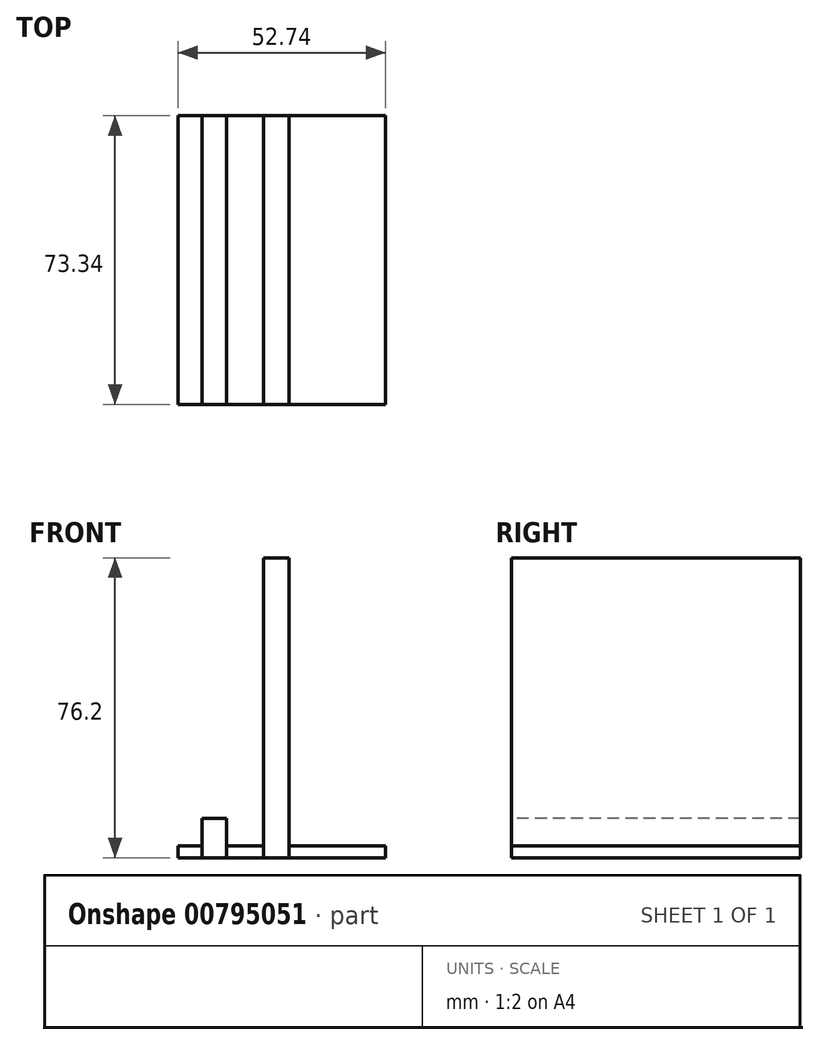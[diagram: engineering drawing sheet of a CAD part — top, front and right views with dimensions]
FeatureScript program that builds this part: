
annotation { "Feature Type Name" : "Feature", "Feature Type Description" : "" }
export const myFeature = defineFeature(function(context is Context, id is Id, definition is map)
    precondition{}
    {
        {
            var Q0;
            Q0=qCreatedBy(makeId("Top.planeOp"),FACE);
            var sketch = newSketch(context, id + "F0", { "sketchPlane" : qUnion([Q0])});
            skLineSegment(sketch, "E0.bottom", {"start": v(-43.9, 42.78) * mm, "end": v(-37.76, 42.78) * mm});
            skLineSegment(sketch, "E0.top", {"start": v(-43.9, -30.56) * mm, "end": v(-37.76, -30.56) * mm});
            skLineSegment(sketch, "E0.left", {"start": v(-43.9, 42.78) * mm, "end": v(-43.9, -30.56) * mm});
            skLineSegment(sketch, "E0.right", {"start": v(-37.76, 42.78) * mm, "end": v(-37.76, -30.56) * mm});
            skLineSegment(sketch, "E1.bottom", {"start": v(-28.3, 42.78) * mm, "end": v(-21.9, 42.78) * mm});
            skLineSegment(sketch, "E1.top", {"start": v(-28.3, -30.56) * mm, "end": v(-21.9, -30.56) * mm});
            skLineSegment(sketch, "E1.left", {"start": v(-28.3, 42.78) * mm, "end": v(-28.3, -30.56) * mm});
            skLineSegment(sketch, "E1.right", {"start": v(-21.9, 42.78) * mm, "end": v(-21.9, -30.56) * mm});
            skLineSegment(sketch, "E2", {"start": v(-43.9, 42.78) * mm, "end": v(-50.05, 42.78) * mm});
            skLineSegment(sketch, "E3", {"start": v(-50.05, 42.78) * mm, "end": v(-50.05, -30.56) * mm});
            skLineSegment(sketch, "E4", {"start": v(-50.05, -30.56) * mm, "end": v(2.69, -30.56) * mm});
            skLineSegment(sketch, "E5", {"start": v(2.69, -30.56) * mm, "end": v(2.69, 42.78) * mm});
            skLineSegment(sketch, "E6", {"start": v(2.69, 42.78) * mm, "end": v(-43.9, 42.78) * mm});
            skSolve(sketch);
        }
        {
            var Q0;
            {var subQ0=sQuery(id+"F0.wireOp",EDGE,"E1.right");Q0=makeQuery(id+"F0.imprint","IMPRINT",FACE,{"disambiguationData":[TD([[makeQuery(id+"F0.imprint","IMPRINT",EDGE,{"derivedFrom":subQ0}),1.0]])]});}
            var Q1;
            {var subQ0=sQuery(id+"F0.wireOp",EDGE,"E0.right");Q1=makeQuery(id+"F0.imprint","IMPRINT",FACE,{"disambiguationData":[TD([[makeQuery(id+"F0.imprint","IMPRINT",EDGE,{"derivedFrom":subQ0}),1.0]])]});}
            var Q2;
            {var subQ0=sQuery(id+"F0.wireOp",EDGE,"E0.left");Q2=makeQuery(id+"F0.imprint","IMPRINT",FACE,{"disambiguationData":[TD([[makeQuery(id+"F0.imprint","IMPRINT",EDGE,{"derivedFrom":subQ0}),-1.0]])]});}
            extrude(context, id + "F1", {"entities" : qUnion([Q0, Q1, Q2]), "depth" : 3 * mm, "offsetDistance" : 25.4 * mm});
        }
        {
            var Q0;
            {var subQ0=sQuery(id+"F0.wireOp",EDGE,"E0.left");Q0=makeQuery(id+"F0.imprint","IMPRINT",FACE,{"disambiguationData":[TD([[makeQuery(id+"F0.imprint","IMPRINT",EDGE,{"derivedFrom":subQ0}),1.0]])]});}
            extrude(context, id + "F2", {"entities" : qUnion([Q0]), "depth" : 10 * mm, "offsetDistance" : 25.4 * mm});
        }
        {
            var Q0;
            {var subQ0=sQuery(id+"F0.wireOp",EDGE,"E1.left");Q0=makeQuery(id+"F0.imprint","IMPRINT",FACE,{"disambiguationData":[TD([[makeQuery(id+"F0.imprint","IMPRINT",EDGE,{"derivedFrom":subQ0}),1.0]])]});}
            extrude(context, id + "F3", {"entities" : qUnion([Q0]), "depth" : 76.2 * mm, "offsetDistance" : 25.4 * mm});
        }
    });
